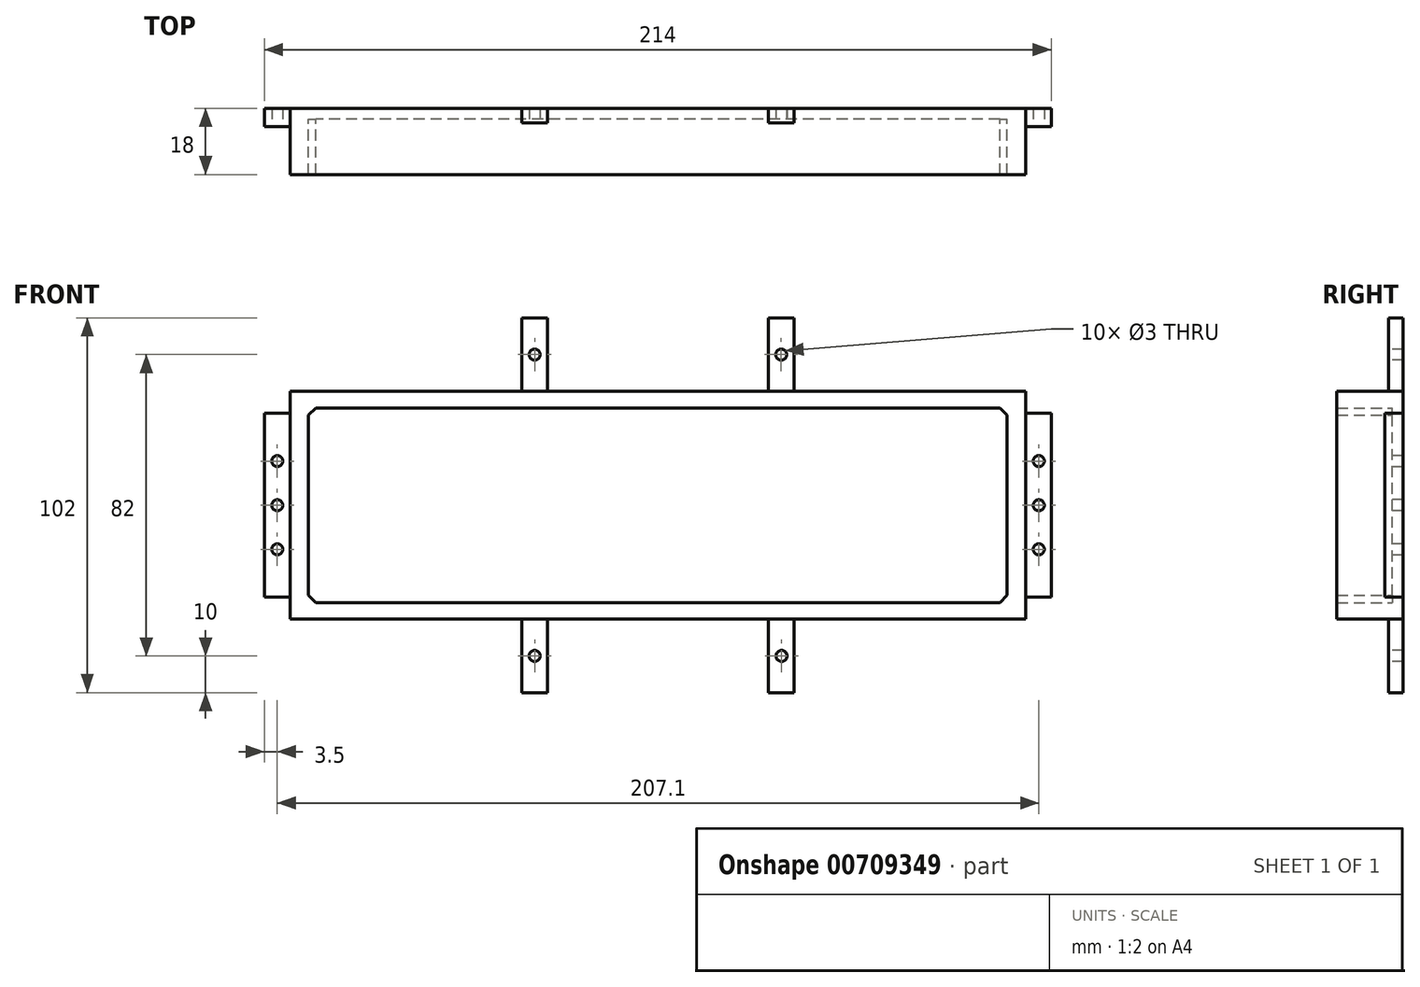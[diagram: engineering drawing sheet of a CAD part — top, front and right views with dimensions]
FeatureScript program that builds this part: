
annotation { "Feature Type Name" : "Feature", "Feature Type Description" : "" }
export const myFeature = defineFeature(function(context is Context, id is Id, definition is map)
    precondition{}
    {
        {
            var Q0;
            Q0=qCreatedBy(makeId("Front.planeOp"),FACE);
            var sketch = newSketch(context, id + "F0", { "sketchPlane" : qUnion([Q0])});
            skLineSegment(sketch, "E0.bottom", {"start": v(95, -26.5) * mm, "end": v(-95, -26.5) * mm});
            skLineSegment(sketch, "E0.top", {"start": v(95, 26.5) * mm, "end": v(-95, 26.5) * mm});
            skLineSegment(sketch, "E0.left", {"start": v(95, -26.5) * mm, "end": v(95, 26.5) * mm});
            skLineSegment(sketch, "E0.right", {"start": v(-95, -26.5) * mm, "end": v(-95, 26.5) * mm});
            skPoint(sketch, "E0.middle", {"position": v(0, 0) * mm});
            skLineSegment(sketch, "E1.bottom", {"start": v(100, -31) * mm, "end": v(-100, -31) * mm});
            skLineSegment(sketch, "E1.top", {"start": v(100, 31) * mm, "end": v(-100, 31) * mm});
            skLineSegment(sketch, "E1.left", {"start": v(100, -31) * mm, "end": v(100, 31) * mm});
            skLineSegment(sketch, "E1.right", {"start": v(-100, -31) * mm, "end": v(-100, 31) * mm});
            skLineSegment(sketch, "E2", {"start": v(-95, 24.5) * mm, "end": v(-93, 26.5) * mm});
            skLineSegment(sketch, "E3", {"start": v(-95, -24.5) * mm, "end": v(-93, -26.5) * mm});
            skLineSegment(sketch, "E4", {"start": v(93, 26.5) * mm, "end": v(95, 24.5) * mm});
            skLineSegment(sketch, "E5", {"start": v(95, -24.5) * mm, "end": v(93, -26.5) * mm});
            skSolve(sketch);
        }
        {
            var Q0;
            {var subQ3=sQuery(id+"F0.wireOp",EDGE,"E3");Q0=makeQuery(id+"F0.imprint","IMPRINT",FACE,{"disambiguationData":[TD([[makeQuery(id+"F0.imprint","IMPRINT",EDGE,{"derivedFrom":subQ3}),-1.0]])]});}
            var Q1;
            {var subQ3=sQuery(id+"F0.wireOp",EDGE,"E2");Q1=makeQuery(id+"F0.imprint","IMPRINT",FACE,{"disambiguationData":[TD([[makeQuery(id+"F0.imprint","IMPRINT",EDGE,{"derivedFrom":subQ3}),1.0]])]});}
            var Q2;
            {var subQ3=sQuery(id+"F0.wireOp",EDGE,"E5");Q2=makeQuery(id+"F0.imprint","IMPRINT",FACE,{"disambiguationData":[TD([[makeQuery(id+"F0.imprint","IMPRINT",EDGE,{"derivedFrom":subQ3}),1.0]])]});}
            var Q3;
            Q3=makeQuery(id+"F0.imprint","IMPRINT",FACE,{"disambiguationData":[TD([[makeQuery(id+"F0.imprint","IMPRINT",EDGE,{"derivedFrom":sQuery(id+"F0.wireOp",EDGE,"E1.bottom")}),-1.0]])]});
            var Q4;
            {var subQ3=sQuery(id+"F0.wireOp",EDGE,"E4");Q4=makeQuery(id+"F0.imprint","IMPRINT",FACE,{"disambiguationData":[TD([[makeQuery(id+"F0.imprint","IMPRINT",EDGE,{"derivedFrom":subQ3}),1.0]])]});}
            extrude(context, id + "F1", {"entities" : qUnion([Q0, Q1, Q2, Q3, Q4]), "depth" : 15 * mm, "offsetDistance" : 25 * mm});
        }
        {
            var Q0;
            Q0=makeQuery(id+"F1.opExtrude","CAP_FACE",FACE,{"disambiguationData":[OSD([sQuery(id+"F0.wireOp",EDGE,"E0.bottom"),sQuery(id+"F0.wireOp",EDGE,"E0.top"),sQuery(id+"F0.wireOp",EDGE,"E0.left"),sQuery(id+"F0.wireOp",EDGE,"E0.right"),sQuery(id+"F0.wireOp",EDGE,"E1.bottom"),sQuery(id+"F0.wireOp",EDGE,"E1.top"),sQuery(id+"F0.wireOp",EDGE,"E1.left"),sQuery(id+"F0.wireOp",EDGE,"E1.right"),sQuery(id+"F0.wireOp",EDGE,"E2"),sQuery(id+"F0.wireOp",EDGE,"E3"),sQuery(id+"F0.wireOp",EDGE,"E4"),sQuery(id+"F0.wireOp",EDGE,"E5")])],"isStart":true});
            var sketch = newSketch(context, id + "F2", { "sketchPlane" : qUnion([Q0])});
            skLineSegment(sketch, "E6.bottom", {"start": v(100, 31) * mm, "end": v(-100, 31) * mm});
            skLineSegment(sketch, "E6.top", {"start": v(100, -31) * mm, "end": v(-100, -31) * mm});
            skLineSegment(sketch, "E6.left", {"start": v(100, 31) * mm, "end": v(100, -31) * mm});
            skLineSegment(sketch, "E6.right", {"start": v(-100, 31) * mm, "end": v(-100, -31) * mm});
            skPoint(sketch, "E6.middle", {"position": v(0, 0) * mm});
            skSolve(sketch);
        }
        {
            var Q0;
            Q0=makeQuery(id+"F2.imprint","IMPRINT",FACE,{"disambiguationData":[TD([[makeQuery(id+"F2.imprint","IMPRINT",EDGE,{"derivedFrom":sQuery(id+"F2.wireOp",EDGE,"E6.bottom")}),-1.0]])]});
            var Q1;
            Q1=makeQuery(id+"F2.imprint","IMPRINT",FACE,{"disambiguationData":[TD([[makeQuery(id+"F2.imprint","IMPRINT",EDGE,{"derivedFrom":makeQuery(id+"F1.opExtrude","CAP_EDGE",EDGE,{"disambiguationData":[OSD([sQuery(id+"F0.wireOp",EDGE,"E0.bottom")])],"isStart":true})}),1.0]])]});
            extrude(context, id + "F3", {"entities" : qUnion([Q0, Q1]), "operationType" : NewBodyOperationType.ADD, "depth" : 3 * mm, "offsetDistance" : 25 * mm});
        }
        {
            var Q0;
            Q0=makeQuery(id+"F3.boolean.opBoolean","MERGE",FACE,{"derivedFrom":[makeQuery(id+"F1.opExtrude","SWEPT_FACE",FACE,{"disambiguationData":[OSD([sQuery(id+"F0.wireOp",EDGE,"E1.right")])]}),makeQuery(id+"F3.opExtrude","SWEPT_FACE",FACE,{"disambiguationData":[OSD([sQuery(id+"F2.wireOp",EDGE,"E6.left")])]})]});
            var sketch = newSketch(context, id + "F4", { "sketchPlane" : qUnion([Q0])});
            skLineSegment(sketch, "E7.bottom", {"start": v(-3, 0) * mm, "end": v(2, 0) * mm});
            skLineSegment(sketch, "E7.top", {"start": v(-3, 25) * mm, "end": v(2, 25) * mm});
            skLineSegment(sketch, "E7.left", {"start": v(-3, 0) * mm, "end": v(-3, 25) * mm});
            skLineSegment(sketch, "E7.right", {"start": v(2, 0) * mm, "end": v(2, 25) * mm});
            skLineSegment(sketch, "E8.top", {"start": v(-3, -25) * mm, "end": v(2, -25) * mm});
            skLineSegment(sketch, "E8.left", {"start": v(-3, 0) * mm, "end": v(-3, -25) * mm});
            skLineSegment(sketch, "E8.right", {"start": v(2, 0) * mm, "end": v(2, -25) * mm});
            skSolve(sketch);
        }
        {
            var Q0;
            Q0=makeQuery(id+"F4.imprint","IMPRINT",FACE,{"disambiguationData":[TD([[makeQuery(id+"F4.imprint","IMPRINT",EDGE,{"derivedFrom":sQuery(id+"F4.wireOp",EDGE,"E7.top")}),-1.0]])]});
            var Q1;
            Q1=makeQuery(id+"F4.imprint","IMPRINT",FACE,{"disambiguationData":[TD([[makeQuery(id+"F4.imprint","IMPRINT",EDGE,{"derivedFrom":sQuery(id+"F4.wireOp",EDGE,"E7.bottom")}),-1.0]])]});
            extrude(context, id + "F5", {"entities" : qUnion([Q0, Q1]), "operationType" : NewBodyOperationType.ADD, "depth" : 7 * mm, "offsetDistance" : 25 * mm});
        }
        {
            var Q0;
            Q0=makeQuery(id+"F5.opExtrude","SWEPT_FACE",FACE,{"disambiguationData":[OSD([sQuery(id+"F4.wireOp",EDGE,"E7.right"),sQuery(id+"F4.wireOp",EDGE,"E8.right")])]});
            var sketch = newSketch(context, id + "F6", { "sketchPlane" : qUnion([Q0])});
            skCircle(sketch, "E9", {"center": v(-103.5, 0) * mm, "radius": 1.5 * mm});
            skCircle(sketch, "E10", {"center": v(-103.5, 12) * mm, "radius": 1.5 * mm});
            skCircle(sketch, "E11", {"center": v(-103.5, -12) * mm, "radius": 1.5 * mm});
            skSolve(sketch);
        }
        {
            var Q0;
            Q0=makeQuery(id+"F6.imprint","IMPRINT",FACE,{"disambiguationData":[TD([[makeQuery(id+"F6.imprint","IMPRINT",EDGE,{"derivedFrom":sQuery(id+"F6.wireOp",EDGE,"E10")}),1.0]])]});
            var Q1;
            Q1=makeQuery(id+"F6.imprint","IMPRINT",FACE,{"disambiguationData":[TD([[makeQuery(id+"F6.imprint","IMPRINT",EDGE,{"derivedFrom":sQuery(id+"F6.wireOp",EDGE,"E9")}),1.0]])]});
            var Q2;
            Q2=makeQuery(id+"F6.imprint","IMPRINT",FACE,{"disambiguationData":[TD([[makeQuery(id+"F6.imprint","IMPRINT",EDGE,{"derivedFrom":sQuery(id+"F6.wireOp",EDGE,"E11")}),1.0]])]});
            extrude(context, id + "F7", {"entities" : qUnion([Q0, Q1, Q2]), "operationType" : NewBodyOperationType.REMOVE, "oppositeDirection" : true, "depth" : 12.6 * mm, "offsetDistance" : 25 * mm});
        }
        {
            var Q0;
            Q0=makeQuery(id+"F3.boolean.opBoolean","MERGE",FACE,{"derivedFrom":[makeQuery(id+"F1.opExtrude","SWEPT_FACE",FACE,{"disambiguationData":[OSD([sQuery(id+"F0.wireOp",EDGE,"E1.left")])]}),makeQuery(id+"F3.opExtrude","SWEPT_FACE",FACE,{"disambiguationData":[OSD([sQuery(id+"F2.wireOp",EDGE,"E6.right")])]})]});
            var sketch = newSketch(context, id + "F8", { "sketchPlane" : qUnion([Q0])});
            skLineSegment(sketch, "E12.bottom", {"start": v(3, 0) * mm, "end": v(-2, 0) * mm});
            skLineSegment(sketch, "E12.top", {"start": v(3, 25) * mm, "end": v(-2, 25) * mm});
            skLineSegment(sketch, "E12.left", {"start": v(3, 0) * mm, "end": v(3, 25) * mm});
            skLineSegment(sketch, "E12.right", {"start": v(-2, 0) * mm, "end": v(-2, 25) * mm});
            skLineSegment(sketch, "E13.top", {"start": v(3, -25) * mm, "end": v(-2, -25) * mm});
            skLineSegment(sketch, "E13.left", {"start": v(3, 0) * mm, "end": v(3, -25) * mm});
            skLineSegment(sketch, "E13.right", {"start": v(-2, 0) * mm, "end": v(-2, -25) * mm});
            skSolve(sketch);
        }
        {
            var Q0;
            Q0=makeQuery(id+"F8.imprint","IMPRINT",FACE,{"disambiguationData":[TD([[makeQuery(id+"F8.imprint","IMPRINT",EDGE,{"derivedFrom":sQuery(id+"F8.wireOp",EDGE,"E12.top")}),1.0]])]});
            var Q1;
            Q1=makeQuery(id+"F8.imprint","IMPRINT",FACE,{"disambiguationData":[TD([[makeQuery(id+"F8.imprint","IMPRINT",EDGE,{"derivedFrom":sQuery(id+"F8.wireOp",EDGE,"E12.bottom")}),1.0]])]});
            extrude(context, id + "F9", {"entities" : qUnion([Q0, Q1]), "operationType" : NewBodyOperationType.ADD, "depth" : 7 * mm, "offsetDistance" : 25 * mm});
        }
        {
            var Q0;
            Q0=makeQuery(id+"F9.opExtrude","SWEPT_FACE",FACE,{"disambiguationData":[OSD([sQuery(id+"F8.wireOp",EDGE,"E12.right"),sQuery(id+"F8.wireOp",EDGE,"E13.right")])]});
            var sketch = newSketch(context, id + "F10", { "sketchPlane" : qUnion([Q0])});
            skCircle(sketch, "E14", {"center": v(103.6, 0) * mm, "radius": 1.5 * mm});
            skPoint(sketch, "E14.centerSnap0", {"position": v(100, 0) * mm});
            skCircle(sketch, "E15", {"center": v(103.6, 12) * mm, "radius": 1.5 * mm});
            skCircle(sketch, "E16", {"center": v(103.6, -12) * mm, "radius": 1.5 * mm});
            skSolve(sketch);
        }
        {
            var Q0;
            Q0=makeQuery(id+"F10.imprint","IMPRINT",FACE,{"disambiguationData":[TD([[makeQuery(id+"F10.imprint","IMPRINT",EDGE,{"derivedFrom":sQuery(id+"F10.wireOp",EDGE,"E14")}),1.0]])]});
            var Q1;
            Q1=makeQuery(id+"F10.imprint","IMPRINT",FACE,{"disambiguationData":[TD([[makeQuery(id+"F10.imprint","IMPRINT",EDGE,{"derivedFrom":sQuery(id+"F10.wireOp",EDGE,"E15")}),1.0]])]});
            var Q2;
            Q2=makeQuery(id+"F10.imprint","IMPRINT",FACE,{"disambiguationData":[TD([[makeQuery(id+"F10.imprint","IMPRINT",EDGE,{"derivedFrom":sQuery(id+"F10.wireOp",EDGE,"E16")}),1.0]])]});
            extrude(context, id + "F11", {"entities" : qUnion([Q0, Q1, Q2]), "operationType" : NewBodyOperationType.REMOVE, "oppositeDirection" : true, "depth" : 25 * mm, "offsetDistance" : 25 * mm});
        }
        {
            var Q0;
            Q0=makeQuery(id+"F3.boolean.opBoolean","MERGE",FACE,{"derivedFrom":[makeQuery(id+"F1.opExtrude","SWEPT_FACE",FACE,{"disambiguationData":[OSD([sQuery(id+"F0.wireOp",EDGE,"E1.top")])]}),makeQuery(id+"F3.opExtrude","SWEPT_FACE",FACE,{"disambiguationData":[OSD([sQuery(id+"F2.wireOp",EDGE,"E6.bottom")])]})]});
            var sketch = newSketch(context, id + "F12", { "sketchPlane" : qUnion([Q0])});
            skLineSegment(sketch, "E17.bottom", {"start": v(-37, 3) * mm, "end": v(-30, 3) * mm});
            skLineSegment(sketch, "E17.top", {"start": v(-37, -1) * mm, "end": v(-30, -1) * mm});
            skLineSegment(sketch, "E17.left", {"start": v(-37, 3) * mm, "end": v(-37, -1) * mm});
            skLineSegment(sketch, "E17.right", {"start": v(-30, 3) * mm, "end": v(-30, -1) * mm});
            skLineSegment(sketch, "E18.bottom", {"start": v(30, 3) * mm, "end": v(37, 3) * mm});
            skLineSegment(sketch, "E18.top", {"start": v(30, -1) * mm, "end": v(37, -1) * mm});
            skLineSegment(sketch, "E18.left", {"start": v(30, 3) * mm, "end": v(30, -1) * mm});
            skLineSegment(sketch, "E18.right", {"start": v(37, 3) * mm, "end": v(37, -1) * mm});
            skSolve(sketch);
        }
        {
            var Q0;
            Q0=makeQuery(id+"F12.imprint","IMPRINT",FACE,{"disambiguationData":[TD([[makeQuery(id+"F12.imprint","IMPRINT",EDGE,{"derivedFrom":sQuery(id+"F12.wireOp",EDGE,"E17.bottom")}),1.0]])]});
            var Q1;
            Q1=makeQuery(id+"F12.imprint","IMPRINT",FACE,{"disambiguationData":[TD([[makeQuery(id+"F12.imprint","IMPRINT",EDGE,{"derivedFrom":sQuery(id+"F12.wireOp",EDGE,"E18.bottom")}),1.0]])]});
            extrude(context, id + "F13", {"entities" : qUnion([Q0, Q1]), "operationType" : NewBodyOperationType.ADD, "depth" : 20 * mm, "offsetDistance" : 25 * mm});
        }
        {
            var Q0;
            Q0=makeQuery(id+"F13.opExtrude","SWEPT_FACE",FACE,{"disambiguationData":[OSD([sQuery(id+"F12.wireOp",EDGE,"E17.top")])]});
            var sketch = newSketch(context, id + "F14", { "sketchPlane" : qUnion([Q0])});
            skCircle(sketch, "E19", {"center": v(-33.5, 41) * mm, "radius": 1.5 * mm});
            skPoint(sketch, "E19.centerSnap0", {"position": v(-33.5, 31) * mm});
            skPoint(sketch, "E19.centerSnap1", {"position": v(-30, 41) * mm});
            skCircle(sketch, "E20", {"center": v(33.55, 41) * mm, "radius": 1.5 * mm});
            skSolve(sketch);
        }
        {
            var Q0;
            Q0=makeQuery(id+"F14.imprint","IMPRINT",FACE,{"disambiguationData":[TD([[makeQuery(id+"F14.imprint","IMPRINT",EDGE,{"derivedFrom":sQuery(id+"F14.wireOp",EDGE,"E19")}),1.0]])]});
            var Q1;
            Q1=makeQuery(id+"F14.imprint","IMPRINT",FACE,{"disambiguationData":[TD([[makeQuery(id+"F14.imprint","IMPRINT",EDGE,{"derivedFrom":sQuery(id+"F14.wireOp",EDGE,"E20")}),1.0]])]});
            extrude(context, id + "F15", {"entities" : qUnion([Q0, Q1]), "operationType" : NewBodyOperationType.REMOVE, "oppositeDirection" : true, "depth" : 25 * mm, "offsetDistance" : 25 * mm});
        }
        {
            var Q0;
            Q0=makeQuery(id+"F3.boolean.opBoolean","MERGE",FACE,{"derivedFrom":[makeQuery(id+"F1.opExtrude","SWEPT_FACE",FACE,{"disambiguationData":[OSD([sQuery(id+"F0.wireOp",EDGE,"E1.bottom")])]}),makeQuery(id+"F3.opExtrude","SWEPT_FACE",FACE,{"disambiguationData":[OSD([sQuery(id+"F2.wireOp",EDGE,"E6.top")])]})]});
            var sketch = newSketch(context, id + "F16", { "sketchPlane" : qUnion([Q0])});
            skLineSegment(sketch, "E21.bottom", {"start": v(-37, -3) * mm, "end": v(-30, -3) * mm});
            skLineSegment(sketch, "E21.top", {"start": v(-37, 1) * mm, "end": v(-30, 1) * mm});
            skLineSegment(sketch, "E21.left", {"start": v(-37, -3) * mm, "end": v(-37, 1) * mm});
            skLineSegment(sketch, "E21.right", {"start": v(-30, -3) * mm, "end": v(-30, 1) * mm});
            skLineSegment(sketch, "E22.bottom", {"start": v(30, -3) * mm, "end": v(37, -3) * mm});
            skLineSegment(sketch, "E22.top", {"start": v(30, 1) * mm, "end": v(37, 1) * mm});
            skLineSegment(sketch, "E22.left", {"start": v(30, -3) * mm, "end": v(30, 1) * mm});
            skLineSegment(sketch, "E22.right", {"start": v(37, -3) * mm, "end": v(37, 1) * mm});
            skSolve(sketch);
        }
        {
            var Q0;
            Q0=makeQuery(id+"F16.imprint","IMPRINT",FACE,{"disambiguationData":[TD([[makeQuery(id+"F16.imprint","IMPRINT",EDGE,{"derivedFrom":sQuery(id+"F16.wireOp",EDGE,"E21.bottom")}),-1.0]])]});
            var Q1;
            Q1=makeQuery(id+"F16.imprint","IMPRINT",FACE,{"disambiguationData":[TD([[makeQuery(id+"F16.imprint","IMPRINT",EDGE,{"derivedFrom":sQuery(id+"F16.wireOp",EDGE,"E22.bottom")}),-1.0]])]});
            extrude(context, id + "F17", {"entities" : qUnion([Q0, Q1]), "operationType" : NewBodyOperationType.ADD, "depth" : 20 * mm, "offsetDistance" : 25 * mm});
        }
        {
            var Q0;
            Q0=makeQuery(id+"F17.opExtrude","SWEPT_FACE",FACE,{"disambiguationData":[OSD([sQuery(id+"F16.wireOp",EDGE,"E21.top")])]});
            var sketch = newSketch(context, id + "F18", { "sketchPlane" : qUnion([Q0])});
            skCircle(sketch, "E23", {"center": v(-33.5, -41) * mm, "radius": 1.5 * mm});
            skPoint(sketch, "E23.centerSnap0", {"position": v(-30, -41) * mm});
            skPoint(sketch, "E23.centerSnap1", {"position": v(-33.5, -51) * mm});
            skCircle(sketch, "E24", {"center": v(33.63, -41) * mm, "radius": 1.5 * mm});
            skSolve(sketch);
        }
        {
            var Q0;
            Q0=makeQuery(id+"F18.imprint","IMPRINT",FACE,{"disambiguationData":[TD([[makeQuery(id+"F18.imprint","IMPRINT",EDGE,{"derivedFrom":sQuery(id+"F18.wireOp",EDGE,"E23")}),1.0]])]});
            var Q1;
            Q1=makeQuery(id+"F18.imprint","IMPRINT",FACE,{"disambiguationData":[TD([[makeQuery(id+"F18.imprint","IMPRINT",EDGE,{"derivedFrom":sQuery(id+"F18.wireOp",EDGE,"E24")}),1.0]])]});
            extrude(context, id + "F19", {"entities" : qUnion([Q0, Q1]), "operationType" : NewBodyOperationType.REMOVE, "oppositeDirection" : true, "depth" : 25 * mm, "offsetDistance" : 25 * mm});
        }
    });
